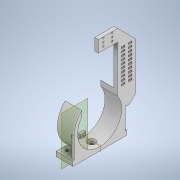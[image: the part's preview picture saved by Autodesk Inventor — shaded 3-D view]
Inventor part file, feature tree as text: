
AUTODESK INVENTOR PART (.ipt)
format: ipt  version: 2020 (Build 240168000, 168)  size: 344,576 bytes
history: native  units: in
note: dims shown in document units (in); Inventor stores cm internally (conversion verified against a paired STEP export)
features: extrude x10, sketch x9, chamfer x3, plane x2, pattern_linear x1, mirror x1
ambient origin geometry x8: Origin, YZ Plane, XZ Plane, XY Plane, X Axis, Y Axis, Z Axis, Center Point
bodies: Solid1 (feature_tree)
feature tree (26):
  extrude  "Extrusion1"  Depth=2.15in
  extrude  "Extrusion2"  Depth=0.7in TaperAngle=0.0deg
  extrude  "Extrusion3"  Depth=0.75in
  extrude  "Extrusion4"  Depth=0.15in TaperAngle=0.0deg
  extrude  "Extrusion5"  Depth=2.25in
  chamfer  "Chamfer1"  Distance=0.25in
  extrude  "Extrusion6"  Depth=0.25in
  pattern_linear  "Rectangular Pattern1"  Spacing1=0.2in  [1 undecoded]
  extrude  "Extrusion7"  Depth=0.25in TaperAngle=0.0deg
  plane  "Work Plane1"
  extrude  "Extrusion8"  Depth=0.15in
  plane  "Work Plane2"
  mirror  "Mirror1"
  extrude  "Extrusion9"  Depth=0.3in
  chamfer  "Chamfer2"  Distance=0.25in
  extrude  "Extrusion10"  TaperAngle=0.0deg  [1 undecoded]
  chamfer  "Chamfer3"  Distance=0.25in
  sketch  "Sketch1"  dims[d0=1.85in d1=2.15in]
  sketch  "Sketch2"  dims[d2=0.2in d3=0.7in d4=0.0in]
  sketch  "Sketch4"  dims[d5=1.5in d6=0.75in]
  sketch  "Sketch5"  dims[d7=2.5in d8=0.15in d9=0.0in]
  sketch  "Sketch6"  dims[d10=0.0in d11=2.25in]
  sketch  "Sketch7"  dims[d12=1.125in]
  sketch  "Sketch8"  dims[d13=0.118in]
  sketch  "Sketch9"  dims[d14=0.118in]
  sketch  "Sketch10"  dims[d15=0.0in d16=0.25in d17=0.25in d18=0.2in d19=0.25in d20=0.0in d21=0.15in d22=0.3in d23=0.25in d24=0.0in d25=0.25in d26=0.0in d27=0.15in d28=0.0in d29=0.25in d30=0.125in d31=45.0deg d32=0.118in d33=0.118in d34=0.2in d35=1.75in d36=0.2in d37=0.065in d38=0.25in d39=0.15in d40=0.15in d41=0.15in d42=0.15in d43=0.15in d44=0.25in d45=0.0in d46=3.937in d48=0.15in d49=0.25in d50=0.3in d51=1.0in d52=0.1in d53=0.0in d54=-0.65in d55=0.1in d56=0.0in d57=-1.125in d58=0.5in d59=0.8in d60=0.3in d61=0.07in d62=0.375in d63=0.07in d64=0.2in d65=0.15in d66=0.0in d67=0.75in d68=0.125in d69=45.0deg d70=0.118in d71=0.35in d72=0.2in d73=0.0in d74=0.1in d75=0.125in d76=45.0deg d77=0.07in d78=0.07in d79=0.15in d80=0.15in d81=0.07in d82=0.07in d83=0.15in d84=0.15in]
note: 2 required parameter values undecoded (feature->parameter linkage not recoverable at this tier; creation-order binding heuristic only, values carry confidence <= 0.55)
